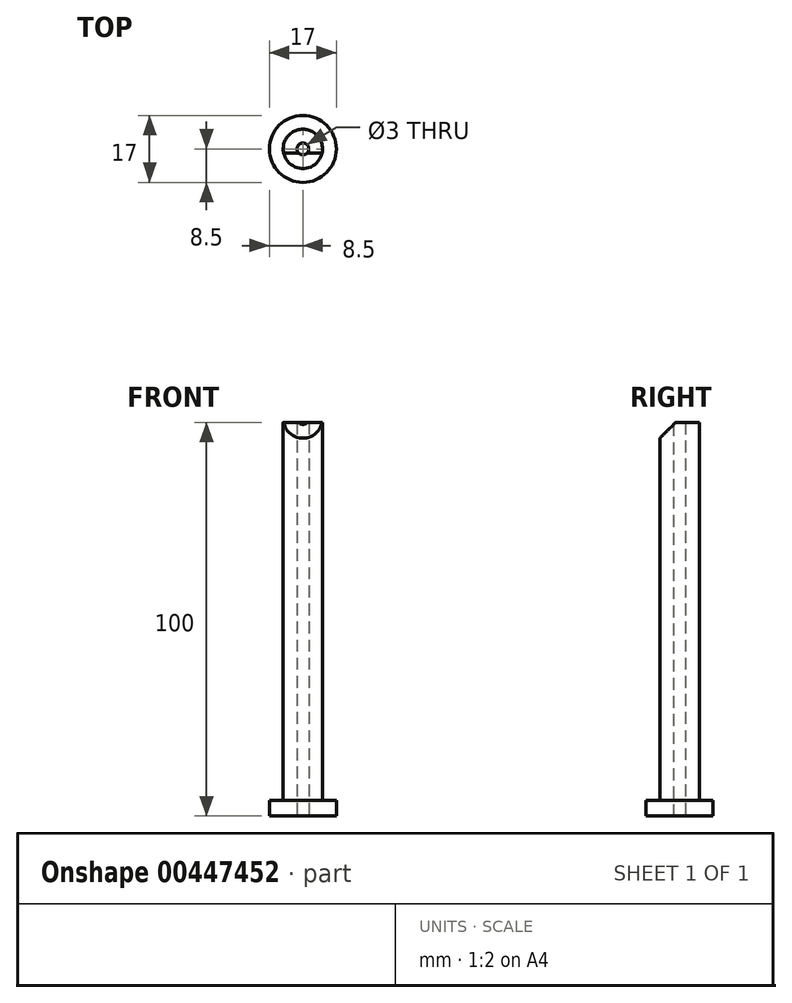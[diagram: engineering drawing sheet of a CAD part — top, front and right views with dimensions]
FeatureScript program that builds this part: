
annotation { "Feature Type Name" : "Feature", "Feature Type Description" : "" }
export const myFeature = defineFeature(function(context is Context, id is Id, definition is map)
    precondition{}
    {
        {
            var Q0;
            Q0=qCreatedBy(makeId("Top.planeOp"),FACE);
            var sketch = newSketch(context, id + "F0", { "sketchPlane" : qUnion([Q0])});
            skCircle(sketch, "E0", {"center": v(0, 0) * mm, "radius": 8.5 * mm});
            skSolve(sketch);
        }
        {
            var Q0;
            Q0=qSketchRegion(id+"F0",true);
            extrude(context, id + "F1", {"entities" : qUnion([Q0]), "depth" : 4 * mm});
        }
        {
            var Q0;
            Q0=qCreatedBy(makeId("Top.planeOp"),FACE);
            var sketch = newSketch(context, id + "F2", { "sketchPlane" : qUnion([Q0])});
            skCircle(sketch, "E1", {"center": v(0, 0) * mm, "radius": 5 * mm});
            skSolve(sketch);
        }
        {
            var Q0;
            Q0=qSketchRegion(id+"F2",true);
            extrude(context, id + "F3", {"entities" : qUnion([Q0]), "operationType" : NewBodyOperationType.ADD, "depth" : 100 * mm});
        }
        {
            var Q0;
            Q0=qCreatedBy(makeId("Right.planeOp"),FACE);
            var sketch = newSketch(context, id + "F4", { "sketchPlane" : qUnion([Q0])});
            skLineSegment(sketch, "E2", {"start": v(-5, 101) * mm, "end": v(-5, 96) * mm});
            skLineSegment(sketch, "E3", {"start": v(-5, 96) * mm, "end": v(0, 101) * mm});
            skLineSegment(sketch, "E4", {"start": v(0, 101) * mm, "end": v(-5, 101) * mm});
            skSolve(sketch);
        }
        {
            var Q0;
            Q0=qSketchRegion(id+"F4",true);
            extrude(context, id + "F5", {"entities" : qUnion([Q0]), "operationType" : NewBodyOperationType.REMOVE, "depth" : 25 * mm, "hasSecondDirection" : true, "secondDirectionOppositeDirection" : true, "secondDirectionDepth" : 25 * mm});
        }
        {
            var Q0;
            Q0=makeQuery(id+"F1.opExtrude","CAP_FACE",FACE,{"disambiguationData":[OSD([sQuery(id+"F0.wireOp",EDGE,"E0")])],"isStart":true});
            var sketch = newSketch(context, id + "F6", { "sketchPlane" : qUnion([Q0])});
            skCircle(sketch, "E5", {"center": v(0, 0) * mm, "radius": 1.5 * mm});
            skSolve(sketch);
        }
        {
            var Q0;
            Q0 = qSketchRegion(id + "F6", true);
            extrude(context, id + "F7", {"entities" : qUnion([Q0]), "operationType" : NewBodyOperationType.REMOVE, "oppositeDirection" : true, "depth" : 130.6 * mm});
        }
    });
